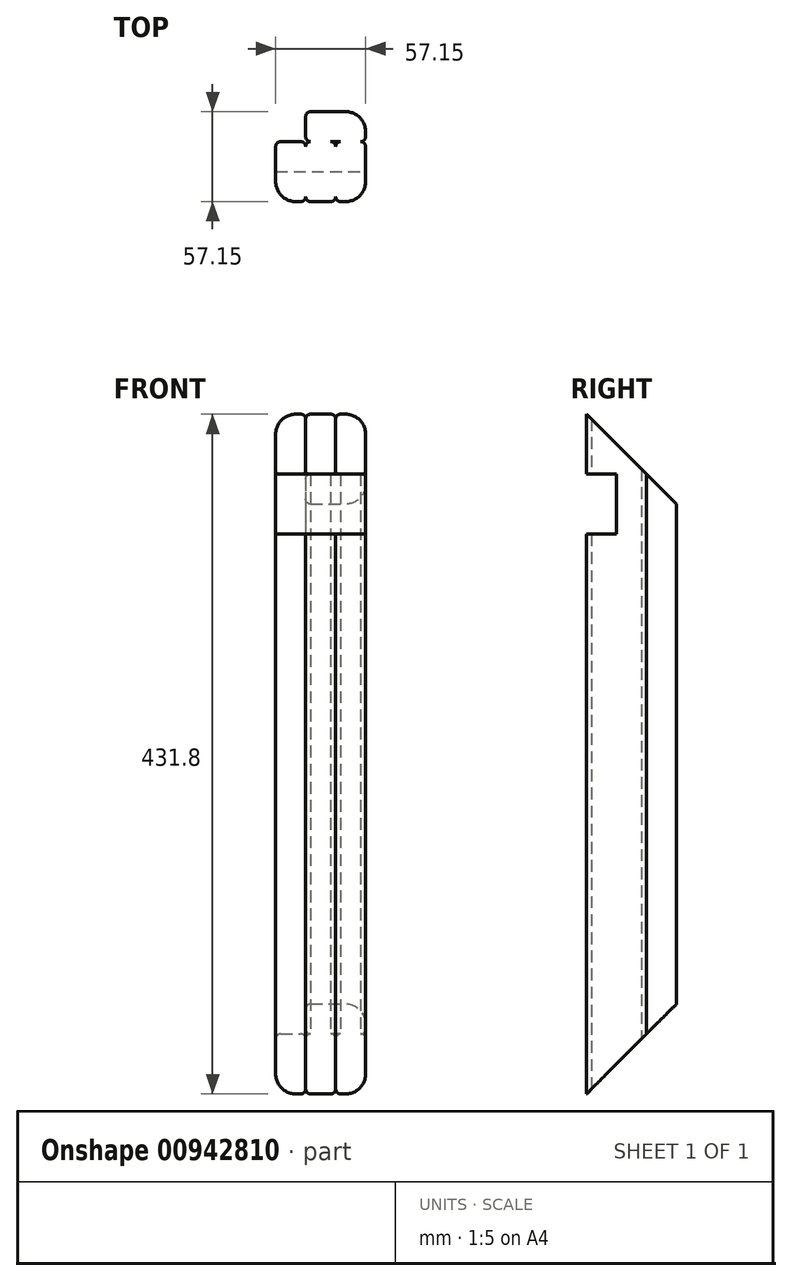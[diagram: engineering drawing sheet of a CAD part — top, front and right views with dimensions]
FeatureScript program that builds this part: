
annotation { "Feature Type Name" : "Feature", "Feature Type Description" : "" }
export const myFeature = defineFeature(function(context is Context, id is Id, definition is map)
    precondition{}
    {
        {
            var Q0;
            Q0=qCreatedBy(makeId("Top.planeOp"),FACE);
            var sketch = newSketch(context, id + "F0", { "sketchPlane" : qUnion([Q0])});
            skLineSegment(sketch, "E0.bottom", {"start": v(12.7, 0) * mm, "end": v(15.9, 0) * mm});
            skLineSegment(sketch, "E0.top", {"start": v(3.15, 38.1) * mm, "end": v(15.9, 38.1) * mm});
            skLineSegment(sketch, "E0.left", {"start": v(0, 12.7) * mm, "end": v(0, 34.95) * mm});
            skLineSegment(sketch, "E0.right", {"start": v(19.05, 3.15) * mm, "end": v(19.05, 34.95) * mm});
            skPoint(sketch, "E1.visualSharp", {"position": v(0, 38.1) * mm});
            skArc(sketch, "E1.filletArc", {"start": v(3.15, 38.1) * mm, "mid": v(0.92, 37.18) * mm, "end": v(0, 34.95) * mm});
            skPoint(sketch, "E2.visualSharp", {"position": v(19.05, 38.1) * mm});
            skArc(sketch, "E2.filletArc", {"start": v(19.05, 34.95) * mm, "mid": v(18.13, 37.18) * mm, "end": v(15.9, 38.1) * mm});
            skPoint(sketch, "E3.visualSharp", {"position": v(19.05, 0) * mm});
            skArc(sketch, "E3.filletArc", {"start": v(15.9, 0) * mm, "mid": v(18.13, 0.92) * mm, "end": v(19.05, 3.15) * mm});
            skPoint(sketch, "E4.visualSharp", {"position": v(0, 0) * mm});
            skArc(sketch, "E4.filletArc", {"start": v(0, 12.7) * mm, "mid": v(3.72, 3.72) * mm, "end": v(12.7, 0) * mm});
            skLineSegment(sketch, "E5.bottom", {"start": v(22.2, 0) * mm, "end": v(34.95, 0) * mm});
            skLineSegment(sketch, "E5.top", {"start": v(22.2, 38.1) * mm, "end": v(34.95, 38.1) * mm});
            skLineSegment(sketch, "E5.right", {"start": v(38.1, 3.15) * mm, "end": v(38.1, 34.95) * mm});
            skArc(sketch, "E6.filletArc", {"start": v(22.2, 38.1) * mm, "mid": v(19.97, 37.18) * mm, "end": v(19.05, 34.95) * mm});
            skPoint(sketch, "E7.visualSharp", {"position": v(38.1, 38.1) * mm});
            skArc(sketch, "E7.filletArc", {"start": v(38.1, 34.95) * mm, "mid": v(37.18, 37.18) * mm, "end": v(34.95, 38.1) * mm});
            skPoint(sketch, "E8.visualSharp", {"position": v(38.1, 0) * mm});
            skArc(sketch, "E8.filletArc", {"start": v(34.95, 0) * mm, "mid": v(37.18, 0.92) * mm, "end": v(38.1, 3.15) * mm});
            skArc(sketch, "E9.filletArc", {"start": v(19.05, 3.15) * mm, "mid": v(19.97, 0.92) * mm, "end": v(22.2, 0) * mm});
            skLineSegment(sketch, "E10.bottom", {"start": v(41.25, 0) * mm, "end": v(44.45, 0) * mm});
            skLineSegment(sketch, "E10.top", {"start": v(41.25, 38.1) * mm, "end": v(54, 38.1) * mm});
            skLineSegment(sketch, "E10.right", {"start": v(57.15, 12.7) * mm, "end": v(57.15, 34.95) * mm});
            skArc(sketch, "E11.filletArc", {"start": v(41.25, 38.1) * mm, "mid": v(39.02, 37.18) * mm, "end": v(38.1, 34.95) * mm});
            skPoint(sketch, "E12.visualSharp", {"position": v(57.15, 38.1) * mm});
            skArc(sketch, "E12.filletArc", {"start": v(57.15, 34.95) * mm, "mid": v(56.23, 37.18) * mm, "end": v(54, 38.1) * mm});
            skPoint(sketch, "E13.visualSharp", {"position": v(57.15, 0) * mm});
            skArc(sketch, "E13.filletArc", {"start": v(44.45, 0) * mm, "mid": v(53.43, 3.72) * mm, "end": v(57.15, 12.7) * mm});
            skArc(sketch, "E14.filletArc", {"start": v(38.1, 3.15) * mm, "mid": v(39.02, 0.92) * mm, "end": v(41.25, 0) * mm});
            skLineSegment(sketch, "E15.bottom", {"start": v(57.15, 41.25) * mm, "end": v(57.15, 44.45) * mm});
            skLineSegment(sketch, "E15.top", {"start": v(19.05, 41.25) * mm, "end": v(19.05, 54) * mm});
            skLineSegment(sketch, "E15.left", {"start": v(54, 38.1) * mm, "end": v(22.2, 38.1) * mm});
            skLineSegment(sketch, "E15.right", {"start": v(44.45, 57.15) * mm, "end": v(22.2, 57.15) * mm});
            skArc(sketch, "E16.filletArc", {"start": v(19.05, 41.25) * mm, "mid": v(19.97, 39.02) * mm, "end": v(22.2, 38.1) * mm});
            skPoint(sketch, "E17.visualSharp", {"position": v(19.05, 57.15) * mm});
            skArc(sketch, "E17.filletArc", {"start": v(22.2, 57.15) * mm, "mid": v(19.97, 56.23) * mm, "end": v(19.05, 54) * mm});
            skPoint(sketch, "E18.visualSharp", {"position": v(57.15, 57.15) * mm});
            skArc(sketch, "E18.filletArc", {"start": v(57.15, 44.45) * mm, "mid": v(53.43, 53.43) * mm, "end": v(44.45, 57.15) * mm});
            skArc(sketch, "E19.filletArc", {"start": v(54, 38.1) * mm, "mid": v(56.23, 39.02) * mm, "end": v(57.15, 41.25) * mm});
            skSolve(sketch);
        }
        {
            var Q0;
            Q0=makeQuery(id+"F0.imprint","IMPRINT",FACE,{"disambiguationData":[TD([[makeQuery(id+"F0.imprint","IMPRINT",EDGE,{"derivedFrom":sQuery(id+"F0.wireOp",EDGE,"E0.bottom")}),1.0]])]});
            var Q1;
            Q1=makeQuery(id+"F0.imprint","IMPRINT",FACE,{"disambiguationData":[TD([[makeQuery(id+"F0.imprint","IMPRINT",EDGE,{"derivedFrom":sQuery(id+"F0.wireOp",EDGE,"E5.bottom")}),1.0]])]});
            var Q2;
            Q2=makeQuery(id+"F0.imprint","IMPRINT",FACE,{"disambiguationData":[TD([[makeQuery(id+"F0.imprint","IMPRINT",EDGE,{"derivedFrom":sQuery(id+"F0.wireOp",EDGE,"E10.bottom")}),1.0]])]});
            var Q3;
            Q3=makeQuery(id+"F0.imprint","IMPRINT",FACE,{"disambiguationData":[TD([[makeQuery(id+"F0.imprint","IMPRINT",EDGE,{"derivedFrom":sQuery(id+"F0.wireOp",EDGE,"E15.bottom")}),1.0]])]});
            extrude(context, id + "F1", {"entities" : qUnion([Q0, Q1, Q2, Q3]), "depth" : 431.8 * mm, "offsetDistance" : 25.4 * mm});
        }
        {
            var Q0;
            Q0=makeQuery(id+"F1.opExtrude","SWEPT_FACE",FACE,{"disambiguationData":[OSD([sQuery(id+"F0.wireOp",EDGE,"E10.right")])]});
            var sketch = newSketch(context, id + "F2", { "sketchPlane" : qUnion([Q0])});
            skLineSegment(sketch, "E20.0", {"start": v(0, 431.8) * mm, "end": v(12.7, 431.8) * mm});
            skLineSegment(sketch, "E21.0", {"start": v(57.15, 431.8) * mm, "end": v(57.15, 0) * mm});
            skLineSegment(sketch, "E22.0", {"start": v(0, 0) * mm, "end": v(12.7, 0) * mm});
            skLineSegment(sketch, "E23", {"start": v(0, 431.8) * mm, "end": v(57.15, 431.8) * mm});
            skLineSegment(sketch, "E24", {"start": v(57.15, 431.8) * mm, "end": v(57.15, 374.65) * mm});
            skLineSegment(sketch, "E25", {"start": v(57.15, 374.65) * mm, "end": v(0, 431.8) * mm});
            skLineSegment(sketch, "E26", {"start": v(0, 0) * mm, "end": v(57.15, 0) * mm});
            skLineSegment(sketch, "E27", {"start": v(57.15, 0) * mm, "end": v(57.15, 57.15) * mm});
            skLineSegment(sketch, "E28", {"start": v(57.15, 57.15) * mm, "end": v(0, 0) * mm});
            skLineSegment(sketch, "E29", {"start": v(57.15, 57.15) * mm, "end": v(57.15, 0) * mm});
            skSolve(sketch);
        }
        {
            var Q0;
            Q0=qSketchRegion(id+"F2",true);
            extrude(context, id + "F3", {"entities" : qUnion([Q0]), "operationType" : NewBodyOperationType.REMOVE, "endBound" : BoundingType.THROUGH_ALL, "oppositeDirection" : true, "depth" : 25.4 * mm, "offsetDistance" : 25.4 * mm});
        }
        {
            var Q0;
            Q0=makeQuery(id+"F1.opExtrude","SWEPT_FACE",FACE,{"disambiguationData":[OSD([sQuery(id+"F0.wireOp",EDGE,"E10.right")])]});
            var sketch = newSketch(context, id + "F4", { "sketchPlane" : qUnion([Q0])});
            skLineSegment(sketch, "E30.bottom", {"start": v(0, 393.7) * mm, "end": v(19.05, 393.7) * mm});
            skLineSegment(sketch, "E30.top", {"start": v(0, 355.6) * mm, "end": v(19.05, 355.6) * mm});
            skLineSegment(sketch, "E30.left", {"start": v(0, 393.7) * mm, "end": v(0, 355.6) * mm});
            skLineSegment(sketch, "E30.right", {"start": v(19.05, 393.7) * mm, "end": v(19.05, 355.6) * mm});
            skSolve(sketch);
        }
        {
            var Q0;
            {var subQ0=sQuery(id+"F4.wireOp",EDGE,"E30.left");Q0=makeQuery(id+"F4.imprint","IMPRINT",FACE,{"disambiguationData":[TD([[makeQuery(id+"F4.imprint","IMPRINT",EDGE,{"derivedFrom":subQ0}),1.0]])]});}
            var Q1;
            {var subQ0=sQuery(id+"F4.wireOp",EDGE,"E30.right");Q1=makeQuery(id+"F4.imprint","IMPRINT",FACE,{"disambiguationData":[TD([[makeQuery(id+"F4.imprint","IMPRINT",EDGE,{"derivedFrom":subQ0}),-1.0]])]});}
            extrude(context, id + "F5", {"entities" : qUnion([Q0, Q1]), "operationType" : NewBodyOperationType.REMOVE, "endBound" : BoundingType.THROUGH_ALL, "oppositeDirection" : true, "depth" : 25.4 * mm, "offsetDistance" : 25.4 * mm});
        }
    });
